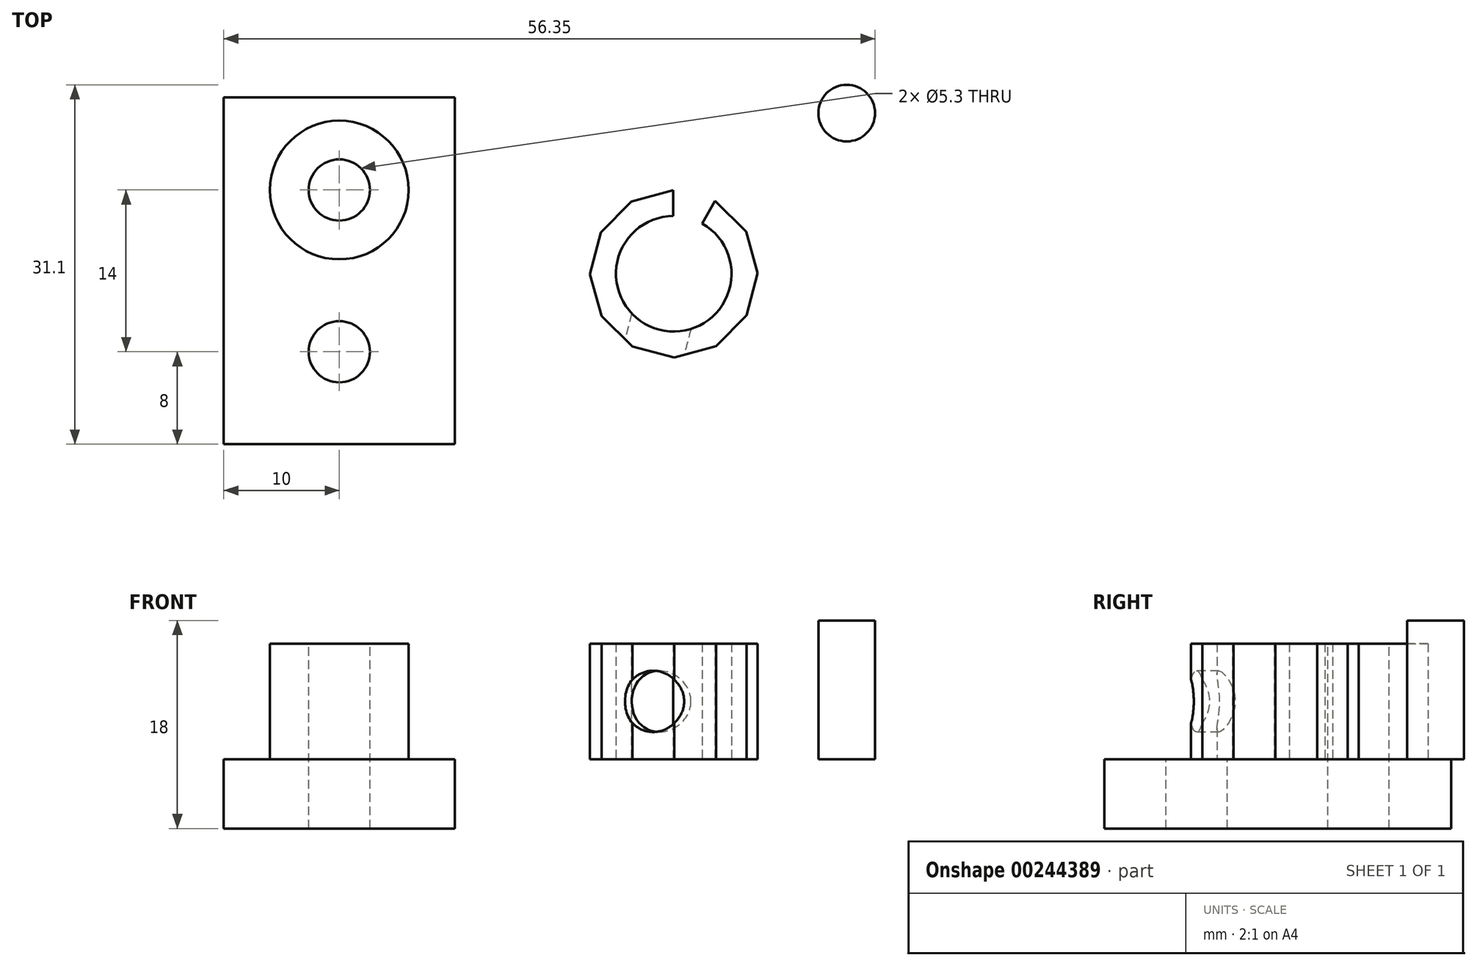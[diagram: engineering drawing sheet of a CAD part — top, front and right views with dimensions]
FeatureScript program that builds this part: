
annotation { "Feature Type Name" : "Feature", "Feature Type Description" : "" }
export const myFeature = defineFeature(function(context is Context, id is Id, definition is map)
    precondition{}
    {
        {
            var Q0;
            Q0=qCreatedBy(makeId("Top.planeOp"),FACE);
            var sketch = newSketch(context, id + "F0", { "sketchPlane" : qUnion([Q0])});
            skLineSegment(sketch, "E0.bottom", {"start": v(-10, 22) * mm, "end": v(10, 22) * mm});
            skLineSegment(sketch, "E0.top", {"start": v(-10, -8) * mm, "end": v(10, -8) * mm});
            skLineSegment(sketch, "E0.left", {"start": v(-10, 22) * mm, "end": v(-10, -8) * mm});
            skLineSegment(sketch, "E0.right", {"start": v(10, 22) * mm, "end": v(10, -8) * mm});
            skCircle(sketch, "E1", {"center": v(0, 0) * mm, "radius": 2.65 * mm});
            skLineSegment(sketch, "E2", {"start": v(-10, 0) * mm, "end": v(10, 0) * mm, "construction": true});
            skLineSegment(sketch, "E3", {"start": v(-10, 14) * mm, "end": v(10, 14) * mm, "construction": true});
            skCircle(sketch, "E4", {"center": v(0, 14) * mm, "radius": 2.65 * mm});
            skCircle(sketch, "E5", {"center": v(0, 14) * mm, "radius": 6 * mm});
            skArc(sketch, "E6", {"start": v(28.9, 11.75) * mm, "mid": v(27.67, 1.91) * mm, "end": v(31.4, 11.1) * mm});
            skArc(sketch, "E7.cCircle", {"start": v(28.96, 13.75) * mm, "mid": v(27.16, -0.02) * mm, "end": v(32.34, 12.87) * mm, "construction": true});
            skLineSegment(sketch, "E7.0", {"start": v(32.6, 0.5) * mm, "end": v(28.98, -0.5) * mm});
            skLineSegment(sketch, "E7.1", {"start": v(28.98, -0.5) * mm, "end": v(25.35, 0.45) * mm});
            skLineSegment(sketch, "E7.2", {"start": v(25.35, 0.45) * mm, "end": v(22.68, 3.1) * mm});
            skLineSegment(sketch, "E7.3", {"start": v(22.68, 3.1) * mm, "end": v(21.69, 6.7) * mm});
            skLineSegment(sketch, "E7.4", {"start": v(21.69, 6.7) * mm, "end": v(22.64, 10.34) * mm});
            skLineSegment(sketch, "E7.5", {"start": v(22.64, 10.34) * mm, "end": v(25.27, 13) * mm});
            skLineSegment(sketch, "E7.6", {"start": v(25.27, 13) * mm, "end": v(28.9, 14) * mm});
            skLineSegment(sketch, "E7.8", {"start": v(32.52, 13.05) * mm, "end": v(35.19, 10.41) * mm});
            skLineSegment(sketch, "E7.9", {"start": v(35.19, 10.41) * mm, "end": v(36.18, 6.8) * mm});
            skLineSegment(sketch, "E7.10", {"start": v(36.18, 6.8) * mm, "end": v(35.23, 3.16) * mm});
            skLineSegment(sketch, "E7.11", {"start": v(35.23, 3.16) * mm, "end": v(32.6, 0.5) * mm});
            skPoint(sketch, "E7.0.midPoint", {"position": v(30.78, 0) * mm});
            skLineSegment(sketch, "E8", {"start": v(28.9, 14) * mm, "end": v(28.96, 13.75) * mm});
            skLineSegment(sketch, "E9", {"start": v(32.52, 13.05) * mm, "end": v(32.34, 12.87) * mm});
            skLineSegment(sketch, "E10", {"start": v(28.9, 14) * mm, "end": v(28.9, 11.75) * mm});
            skLineSegment(sketch, "E11", {"start": v(32.52, 13.05) * mm, "end": v(31.4, 11.1) * mm});
            skCircle(sketch, "E12", {"center": v(43.9, 20.65) * mm, "radius": 2.45 * mm});
            skSolve(sketch);
        }
        {
            var Q0;
            Q0=makeQuery(id+"F0.imprint","IMPRINT",FACE,{"disambiguationData":[TD([[makeQuery(id+"F0.imprint","IMPRINT",EDGE,{"derivedFrom":sQuery(id+"F0.wireOp",EDGE,"E0.bottom")}),-1.0]])]});
            var Q1;
            Q1=makeQuery(id+"F0.imprint","IMPRINT",FACE,{"disambiguationData":[TD([[makeQuery(id+"F0.imprint","IMPRINT",EDGE,{"derivedFrom":sQuery(id+"F0.wireOp",EDGE,"39256127-3d54-457b-a360-4d7563970edb.0")}),1.0]])]});
            var Q2;
            Q2=makeQuery(id+"F0.imprint","IMPRINT",FACE,{"disambiguationData":[TD([[makeQuery(id+"F0.imprint","IMPRINT",EDGE,{"derivedFrom":sQuery(id+"F0.wireOp",EDGE,"E4")}),-1.0]])]});
            extrude(context, id + "F1", {"entities" : qUnion([Q0, Q1, Q2]), "oppositeDirection" : true, "depth" : 6 * mm});
        }
        {
            var Q0;
            Q0=makeQuery(id+"F0.imprint","IMPRINT",FACE,{"disambiguationData":[TD([[makeQuery(id+"F0.imprint","IMPRINT",EDGE,{"derivedFrom":sQuery(id+"F0.wireOp",EDGE,"39256127-3d54-457b-a360-4d7563970edb.0")}),1.0]])]});
            var Q1;
            Q1=makeQuery(id+"F0.imprint","IMPRINT",FACE,{"disambiguationData":[TD([[makeQuery(id+"F0.imprint","IMPRINT",EDGE,{"derivedFrom":sQuery(id+"F0.wireOp",EDGE,"E4")}),-1.0]])]});
            extrude(context, id + "F2", {"entities" : qUnion([Q0, Q1]), "operationType" : NewBodyOperationType.ADD, "depth" : 10 * mm});
        }
        {
            var Q0;
            Q0=makeQuery(id+"F0.imprint","IMPRINT",FACE,{"disambiguationData":[TD([[makeQuery(id+"F0.imprint","IMPRINT",EDGE,{"derivedFrom":sQuery(id+"F0.wireOp",EDGE,"E6")}),-1.0]])]});
            extrude(context, id + "F3", {"entities" : qUnion([Q0]), "depth" : 10 * mm});
        }
        {
            var Q0;
            Q0=makeQuery(id+"F3.opExtrude","SWEPT_FACE",FACE,{"disambiguationData":[OSD([sQuery(id+"F0.wireOp",EDGE,"E7.1")])]});
            var sketch = newSketch(context, id + "F4", { "sketchPlane" : qUnion([Q0])});
            skLineSegment(sketch, "E13.0.0", {"start": v(24.4, 0) * mm, "end": v(28.16, 0) * mm});
            skLineSegment(sketch, "E13.0.1", {"start": v(28.16, 0) * mm, "end": v(28.16, 10) * mm});
            skLineSegment(sketch, "E13.0.2", {"start": v(28.16, 10) * mm, "end": v(24.4, 10) * mm});
            skLineSegment(sketch, "E13.0.3", {"start": v(24.4, 10) * mm, "end": v(24.4, 0) * mm});
            skLineSegment(sketch, "E14", {"start": v(24.4, 10) * mm, "end": v(28.16, 0) * mm, "construction": true});
            skCircle(sketch, "E15", {"center": v(26.28, 5) * mm, "radius": 2.65 * mm});
            skSolve(sketch);
        }
        {
            var Q0;
            {var subQ0=sQuery(id+"F4.wireOp",EDGE,"E15");var subQ1=sQuery(id+"F4.wireOp",EDGE,"E13.0.1");var subQ2=makeQuery(id+"F4.imprint","INTERSECT",VERTEX,{"disambiguationData":[OD(0.0)],"derivedFrom":[subQ1,subQ0]});Q0=makeQuery(id+"F4.imprint","IMPRINT",FACE,{"disambiguationData":[TD([[makeQuery(id+"F4.imprint","IMPRINT",EDGE,{"disambiguationData":[TD([[subQ2,-1.0]])],"derivedFrom":subQ1}),1.0]])]});}
            var Q1;
            {var subQ0=sQuery(id+"F4.wireOp",EDGE,"E15");var subQ1=sQuery(id+"F4.wireOp",EDGE,"E13.0.1");var subQ2=makeQuery(id+"F4.imprint","INTERSECT",VERTEX,{"disambiguationData":[OD(0.0)],"derivedFrom":[subQ1,subQ0]});Q1=makeQuery(id+"F4.imprint","IMPRINT",FACE,{"disambiguationData":[TD([[makeQuery(id+"F4.imprint","IMPRINT",EDGE,{"disambiguationData":[TD([[subQ2,-1.0]])],"derivedFrom":subQ1}),-1.0]])]});}
            var Q2;
            {var subQ0=sQuery(id+"F4.wireOp",EDGE,"E15");var subQ1=sQuery(id+"F4.wireOp",EDGE,"E13.0.3");var subQ2=makeQuery(id+"F4.imprint","INTERSECT",VERTEX,{"disambiguationData":[OD(0.0)],"derivedFrom":[subQ1,subQ0]});Q2=makeQuery(id+"F4.imprint","IMPRINT",FACE,{"disambiguationData":[TD([[makeQuery(id+"F4.imprint","IMPRINT",EDGE,{"disambiguationData":[TD([[subQ2,-1.0]])],"derivedFrom":subQ1}),-1.0]])]});}
            extrude(context, id + "F5", {"entities" : qUnion([Q0, Q1, Q2]), "operationType" : NewBodyOperationType.REMOVE, "endBound" : BoundingType.UP_TO_NEXT, "oppositeDirection" : true, "depth" : 25 * mm});
        }
        {
            var Q0;
            Q0=makeQuery(id+"F0.imprint","IMPRINT",FACE,{"disambiguationData":[TD([[makeQuery(id+"F0.imprint","IMPRINT",EDGE,{"derivedFrom":sQuery(id+"F0.wireOp",EDGE,"E12")}),1.0]])]});
            extrude(context, id + "F6", {"entities" : qUnion([Q0]), "depth" : 12 * mm});
        }
    });
